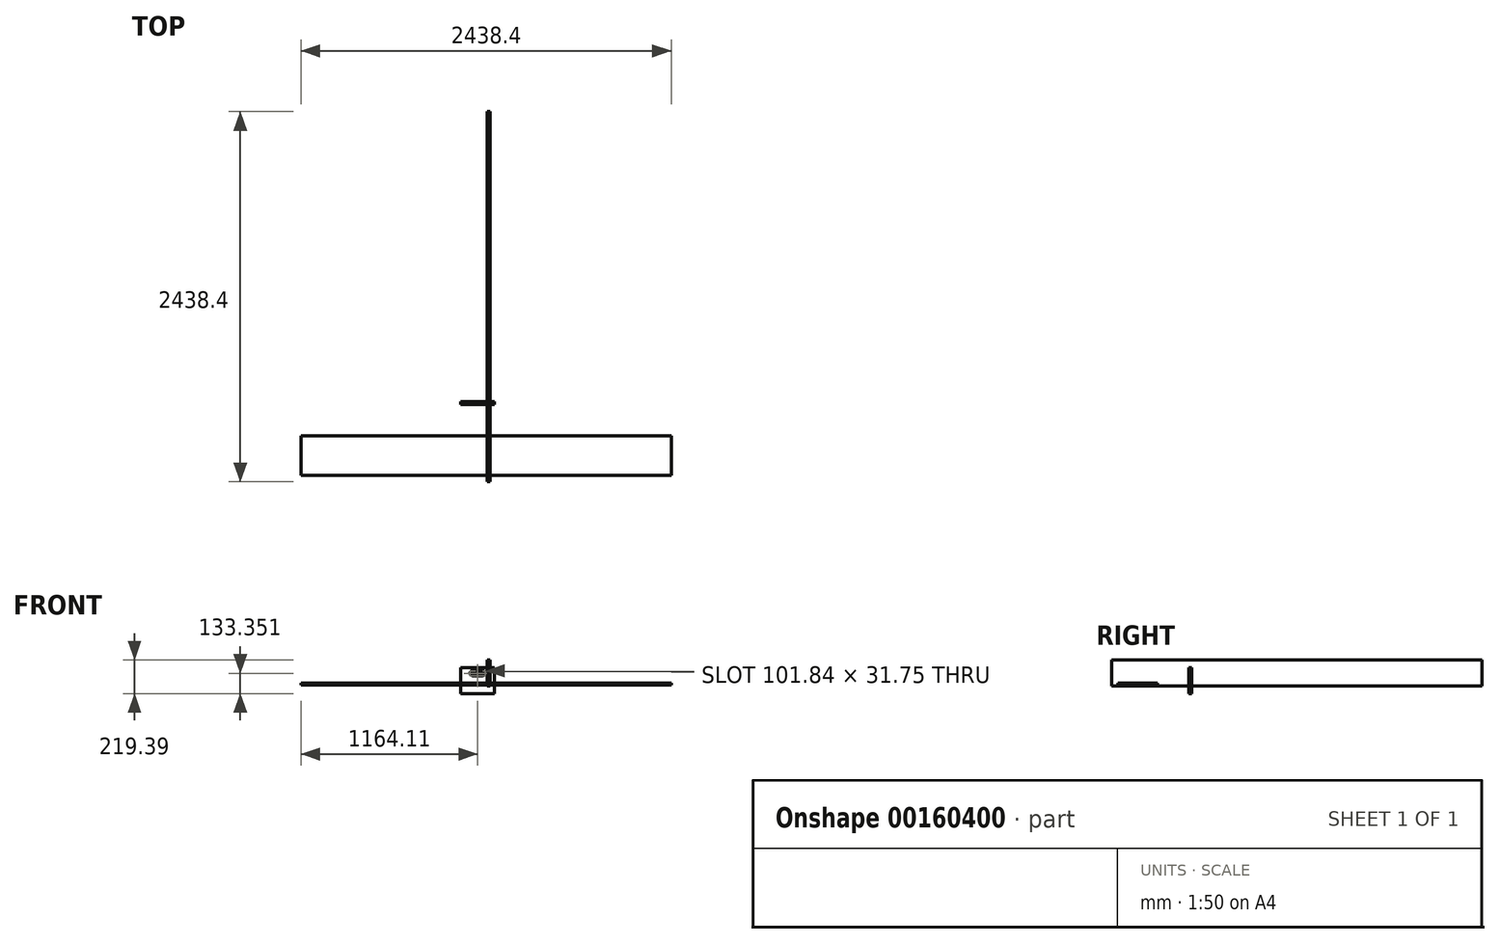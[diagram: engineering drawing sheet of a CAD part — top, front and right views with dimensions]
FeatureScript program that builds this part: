
annotation { "Feature Type Name" : "Feature", "Feature Type Description" : "" }
export const myFeature = defineFeature(function(context is Context, id is Id, definition is map)
    precondition{}
    {
        {
            var Q0;
            Q0=qCreatedBy(makeId("Front.planeOp"),FACE);
            var sketch = newSketch(context, id + "F0", { "sketchPlane" : qUnion([Q0])});
            skLineSegment(sketch, "E0.bottom", {"start": v(-171.8, 115.65) * mm, "end": v(50.44, 115.65) * mm});
            skLineSegment(sketch, "E0.top", {"start": v(-171.8, -55.8) * mm, "end": v(50.44, -55.8) * mm});
            skLineSegment(sketch, "E1.0", {"start": v(-171.8, 115.65) * mm, "end": v(-171.8, -55.8) * mm});
            skLineSegment(sketch, "E2.0", {"start": v(50.44, 115.65) * mm, "end": v(50.44, -55.8) * mm});
            skSolve(sketch);
        }
        {
            var Q0;
            Q0=makeQuery(id+"F0.imprint","IMPRINT",FACE,{"disambiguationData":[TD([[makeQuery(id+"F0.imprint","IMPRINT",EDGE,{"derivedFrom":sQuery(id+"F0.wireOp",EDGE,"E0.bottom")}),-1.0]])]});
            extrude(context, id + "F1", {"entities" : qUnion([Q0]), "depth" : 19.05 * mm});
        }
        {
            var Q0;
            Q0=makeQuery(id+"F1.opExtrude","CAP_FACE",FACE,{"disambiguationData":[OSD([sQuery(id+"F0.wireOp",EDGE,"E0.bottom"),sQuery(id+"F0.wireOp",EDGE,"E0.top"),sQuery(id+"F0.wireOp",EDGE,"E0.left"),sQuery(id+"F0.wireOp",EDGE,"E0.right")])],"isStart":false});
            var sketch = newSketch(context, id + "F2", { "sketchPlane" : qUnion([Q0])});
            skArc(sketch, "E3", {"start": v(-95.6, 93.43) * mm, "mid": v(-111.8, 77.55) * mm, "end": v(-95.6, 61.68) * mm});
            skArc(sketch, "E4", {"start": v(-25.76, 61.68) * mm, "mid": v(-9.96, 77.55) * mm, "end": v(-25.76, 93.43) * mm});
            skLineSegment(sketch, "E5", {"start": v(-95.6, 93.43) * mm, "end": v(-25.76, 93.43) * mm});
            skLineSegment(sketch, "E6", {"start": v(-95.6, 61.68) * mm, "end": v(-25.76, 61.68) * mm});
            skSolve(sketch);
        }
        {
            var Q0;
            Q0=makeQuery(id+"F2.imprint","IMPRINT",FACE,{"disambiguationData":[TD([[makeQuery(id+"F2.imprint","IMPRINT",EDGE,{"derivedFrom":sQuery(id+"F2.wireOp",EDGE,"E3")}),1.0]])]});
            extrude(context, id + "F3", {"entities" : qUnion([Q0]), "operationType" : NewBodyOperationType.REMOVE, "oppositeDirection" : true, "depth" : 19.05 * mm});
        }
        {
            var Q0;
            Q0=qCreatedBy(makeId("Right.planeOp"),FACE);
            var sketch = newSketch(context, id + "F4", { "sketchPlane" : qUnion([Q0])});
            skLineSegment(sketch, "E7.bottom", {"start": v(-526.88, -7.86) * mm, "end": v(1911.52, -7.86) * mm});
            skLineSegment(sketch, "E7.top", {"start": v(-526.88, 163.59) * mm, "end": v(1911.52, 163.59) * mm});
            skLineSegment(sketch, "E7.left", {"start": v(-526.88, -7.86) * mm, "end": v(-526.88, 163.59) * mm});
            skLineSegment(sketch, "E7.right", {"start": v(1911.52, -7.86) * mm, "end": v(1911.52, 163.59) * mm});
            skSolve(sketch);
        }
        {
            var Q0;
            Q0=makeQuery(id+"F4.imprint","IMPRINT",FACE,{"disambiguationData":[TD([[makeQuery(id+"F4.imprint","IMPRINT",EDGE,{"derivedFrom":sQuery(id+"F4.wireOp",EDGE,"E7.bottom")}),1.0]])]});
            extrude(context, id + "F5", {"entities" : qUnion([Q0]), "depth" : 19.05 * mm});
        }
        {
            var Q0;
            Q0=qCreatedBy(makeId("Top.planeOp"),FACE);
            var sketch = newSketch(context, id + "F6", { "sketchPlane" : qUnion([Q0])});
            skLineSegment(sketch, "E8.bottom", {"start": v(1213.41, -485.9) * mm, "end": v(-1224.99, -485.9) * mm});
            skLineSegment(sketch, "E8.top", {"start": v(1213.41, -225.54) * mm, "end": v(-1224.99, -225.54) * mm});
            skLineSegment(sketch, "E8.left", {"start": v(1213.41, -485.9) * mm, "end": v(1213.41, -225.54) * mm});
            skLineSegment(sketch, "E8.right", {"start": v(-1224.99, -485.9) * mm, "end": v(-1224.99, -225.54) * mm});
            skSolve(sketch);
        }
        {
            var Q0;
            Q0=makeQuery(id+"F6.imprint","IMPRINT",FACE,{"disambiguationData":[TD([[makeQuery(id+"F6.imprint","IMPRINT",EDGE,{"derivedFrom":sQuery(id+"F6.wireOp",EDGE,"E8.bottom")}),-1.0]])]});
            extrude(context, id + "F7", {"entities" : qUnion([Q0]), "depth" : 12.7 * mm});
        }
    });
